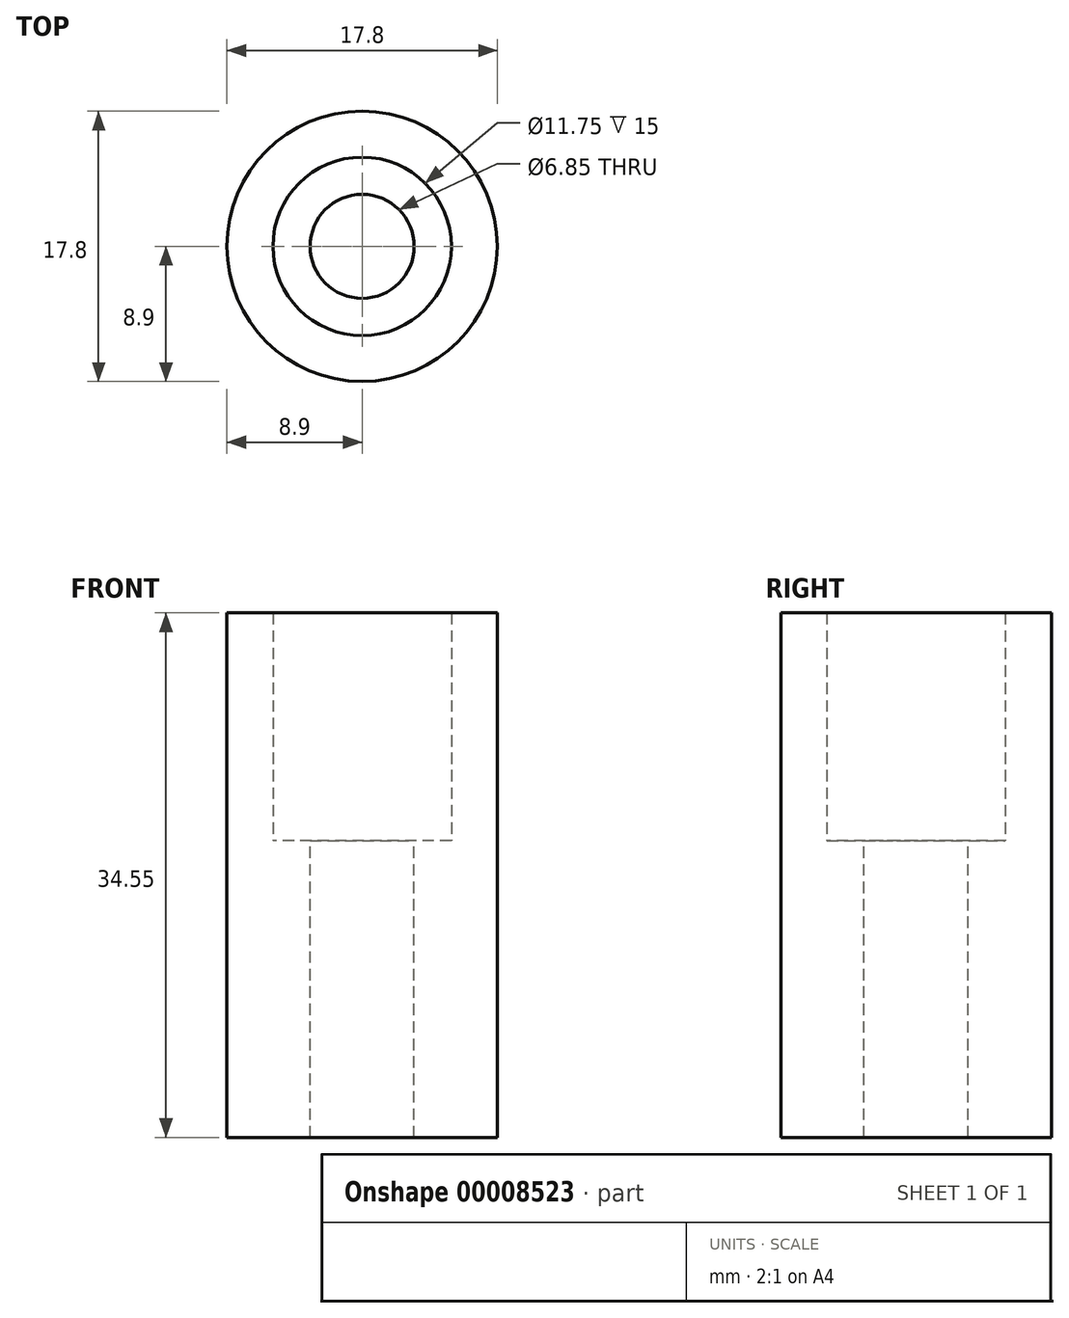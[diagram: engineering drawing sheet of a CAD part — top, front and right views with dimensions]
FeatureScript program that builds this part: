
annotation { "Feature Type Name" : "Feature", "Feature Type Description" : "" }
export const myFeature = defineFeature(function(context is Context, id is Id, definition is map)
    precondition{}
    {
        {
            var Q0;
            Q0=qCreatedBy(makeId("Top.planeOp"),FACE);
            var sketch = newSketch(context, id + "F0", { "sketchPlane" : qUnion([Q0])});
            skCircle(sketch, "E0", {"center": v(0, 0) * mm, "radius": 8.9 * mm});
            skCircle(sketch, "E1", {"center": v(0, 0) * mm, "radius": 5.88 * mm});
            skSolve(sketch);
        }
        {
            var Q0;
            Q0 = qSketchRegion(id + "F0", true);
            extrude(context, id + "F1", {"entities" : qUnion([Q0]), "depth" : 15 * mm});
        }
        {
            var Q0;
            Q0=makeQuery(id+"F1.opExtrude","CAP_FACE",FACE,{"disambiguationData":[OSD([sQuery(id+"F0.wireOp",EDGE,"E0"),sQuery(id+"F0.wireOp",EDGE,"E1")])],"isStart":true});
            var sketch = newSketch(context, id + "F2", { "sketchPlane" : qUnion([Q0])});
            skCircle(sketch, "E2.0", {"center": v(0, 0) * mm, "radius": 8.9 * mm});
            skCircle(sketch, "E3", {"center": v(0, 0) * mm, "radius": 3.43 * mm});
            skSolve(sketch);
        }
        {
            var Q0;
            Q0 = qSketchRegion(id + "F2", true);
            extrude(context, id + "F3", {"entities" : qUnion([Q0]), "operationType" : NewBodyOperationType.ADD, "depth" : 19.55 * mm});
        }
    });
